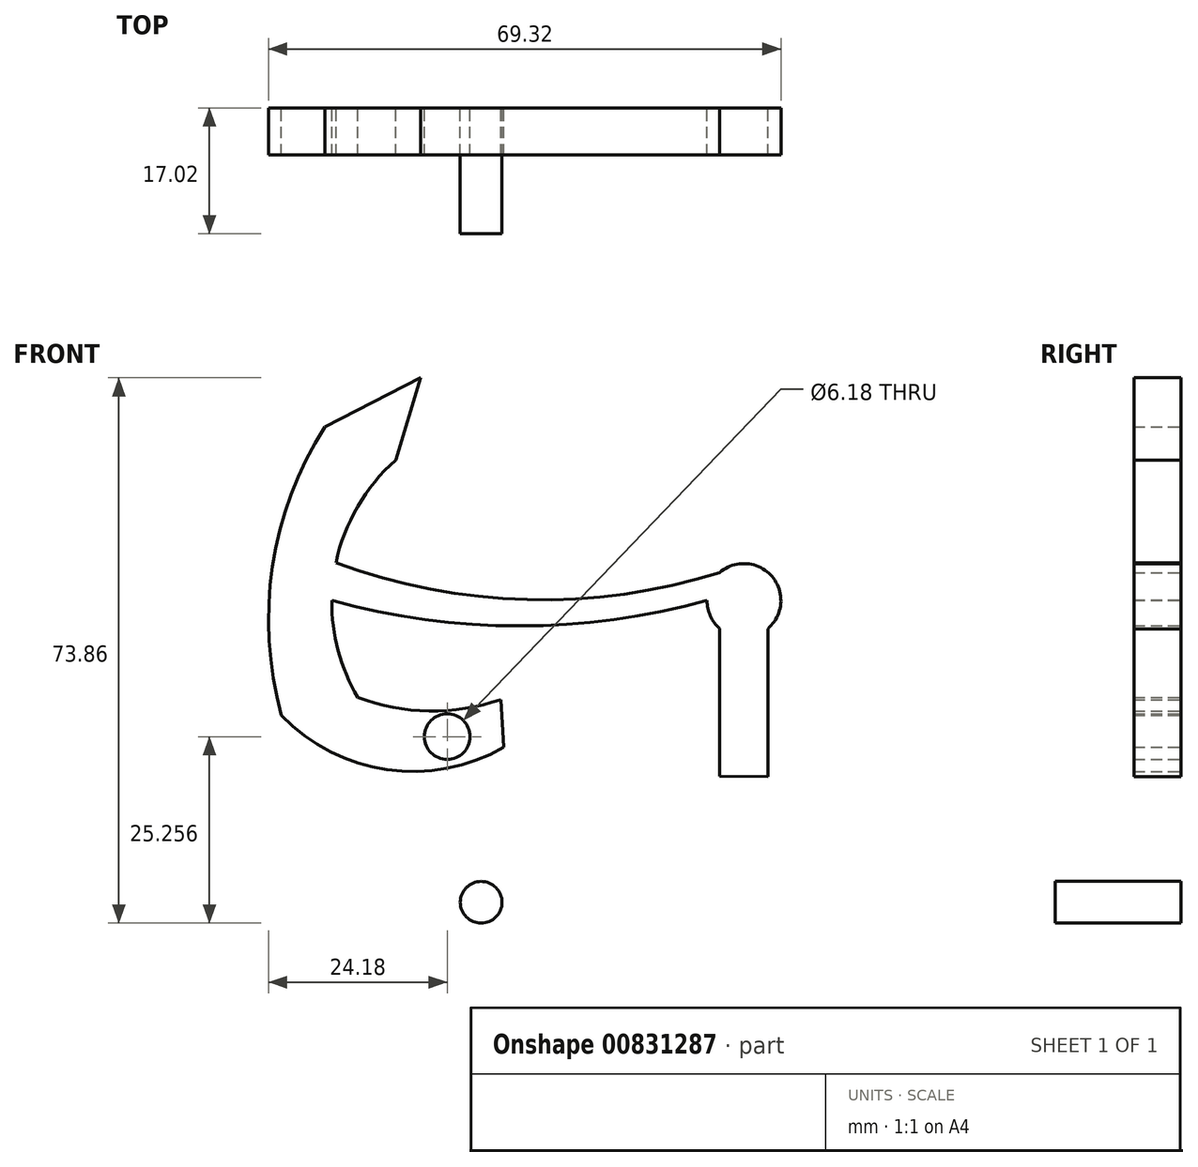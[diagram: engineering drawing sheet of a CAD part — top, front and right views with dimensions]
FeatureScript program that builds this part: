
annotation { "Feature Type Name" : "Feature", "Feature Type Description" : "" }
export const myFeature = defineFeature(function(context is Context, id is Id, definition is map)
    precondition{}
    {
        {
            var Q0;
            Q0=qCreatedBy(makeId("Front.planeOp"),FACE);
            var sketch = newSketch(context, id + "F0", { "sketchPlane" : qUnion([Q0])});
            skCircle(sketch, "E0", {"center": v(0, 0) * mm, "radius": 5 * mm});
            skLineSegment(sketch, "E1", {"start": v(-3.26, -3.79) * mm, "end": v(-3.26, -23.79) * mm});
            skLineSegment(sketch, "E2", {"start": v(3.22, -3.82) * mm, "end": v(3.22, -23.82) * mm});
            skLineSegment(sketch, "E3", {"start": v(-3.26, -23.79) * mm, "end": v(3.22, -23.82) * mm});
            skArc(sketch, "E4", {"start": v(-55.75, 0) * mm, "mid": v(-30.38, -3.43) * mm, "end": v(-5, 0) * mm});
            skArc(sketch, "E5", {"start": v(-58.18, 6.28) * mm, "mid": v(-30.94, 0.19) * mm, "end": v(-3.26, 3.79) * mm});
            skPoint(sketch, "E5.endSnap0", {"position": v(-3.26, -13.79) * mm});
            skLineSegment(sketch, "E6", {"start": v(-58.18, 6.28) * mm, "end": v(-55.75, 0) * mm});
            skArc(sketch, "E7", {"start": v(-56.69, 23.5) * mm, "mid": v(-63.78, 4.61) * mm, "end": v(-62.57, -15.53) * mm});
            skLineSegment(sketch, "E8", {"start": v(-56.69, 23.5) * mm, "end": v(-43.77, 30.17) * mm});
            skLineSegment(sketch, "E9", {"start": v(-43.77, 30.17) * mm, "end": v(-47.12, 19) * mm});
            skLineSegment(sketch, "E10", {"start": v(-47.12, 19) * mm, "end": v(-56.69, 23.5) * mm});
            skArc(sketch, "E11", {"start": v(-47.12, 19) * mm, "mid": v(-55.43, 3.87) * mm, "end": v(-52.27, -13.1) * mm});
            skArc(sketch, "E12", {"start": v(-52.27, -13.1) * mm, "mid": v(-42.6, -14.96) * mm, "end": v(-32.89, -13.41) * mm});
            skArc(sketch, "E13", {"start": v(-62.57, -15.53) * mm, "mid": v(-48.28, -22.9) * mm, "end": v(-32.48, -19.87) * mm});
            skLineSegment(sketch, "E14", {"start": v(-32.89, -13.41) * mm, "end": v(-32.48, -19.87) * mm});
            skCircle(sketch, "E15", {"center": v(-40.14, -18.43) * mm, "radius": 3.09 * mm});
            skCircle(sketch, "E16", {"center": v(-35.55, -40.86) * mm, "radius": 2.83 * mm});
            skCircle(sketch, "E17", {"center": v(-40.14, -18.43) * mm, "radius": 3 * mm});
            skSolve(sketch);
        }
        {
            var Q0;
            Q0=makeQuery(id+"F0.imprint","IMPRINT",FACE,{"disambiguationData":[TD([[makeQuery(id+"F0.imprint","IMPRINT",EDGE,{"derivedFrom":sQuery(id+"F0.wireOp",EDGE,"E8")}),-1.0]])]});
            var Q1;
            Q1=makeQuery(id+"F0.imprint","IMPRINT",FACE,{"disambiguationData":[TD([[makeQuery(id+"F0.imprint","IMPRINT",EDGE,{"derivedFrom":sQuery(id+"F0.wireOp",EDGE,"E7")}),1.0]])]});
            var Q2;
            {var subQ2=sQuery(id+"F0.wireOp",EDGE,"E4");Q2=makeQuery(id+"F0.imprint","IMPRINT",FACE,{"disambiguationData":[TD([[makeQuery(id+"F0.imprint","IMPRINT",EDGE,{"derivedFrom":subQ2}),1.0]])]});}
            var Q3;
            {var subQ0=sQuery(id+"F0.wireOp",EDGE,"E0");var subQ1=makeQuery(id+"F0.imprint","INTERSECT",VERTEX,{"derivedFrom":[subQ0,sQuery(id+"F0.wireOp",EDGE,"E4")]});Q3=makeQuery(id+"F0.imprint","IMPRINT",FACE,{"disambiguationData":[TD([[makeQuery(id+"F0.imprint","IMPRINT",EDGE,{"disambiguationData":[TD([[subQ1,1.0]])],"derivedFrom":subQ0}),1.0]])]});}
            var Q4;
            {var subQ0=sQuery(id+"F0.wireOp",EDGE,"E1");Q4=makeQuery(id+"F0.imprint","IMPRINT",FACE,{"disambiguationData":[TD([[makeQuery(id+"F0.imprint","IMPRINT",EDGE,{"derivedFrom":subQ0}),1.0]])]});}
            var Q5;
            {var subQ0=sQuery(id+"F0.wireOp",EDGE,"E6");Q5=makeQuery(id+"F0.imprint","IMPRINT",FACE,{"disambiguationData":[TD([[makeQuery(id+"F0.imprint","IMPRINT",EDGE,{"derivedFrom":subQ0}),1.0]])]});}
            extrude(context, id + "F1", {"entities" : qUnion([Q0, Q1, Q2, Q3, Q4, Q5]), "depth" : 6.35 * mm, "offsetDistance" : 25.4 * mm});
        }
        {
            var Q0;
            Q0=makeQuery(id+"F0.imprint","IMPRINT",FACE,{"disambiguationData":[TD([[makeQuery(id+"F0.imprint","IMPRINT",EDGE,{"derivedFrom":sQuery(id+"F0.wireOp",EDGE,"E16")}),1.0]])]});
            extrude(context, id + "F2", {"entities" : qUnion([Q0]), "depth" : 17.02 * mm, "offsetDistance" : 25.4 * mm});
        }
    });
